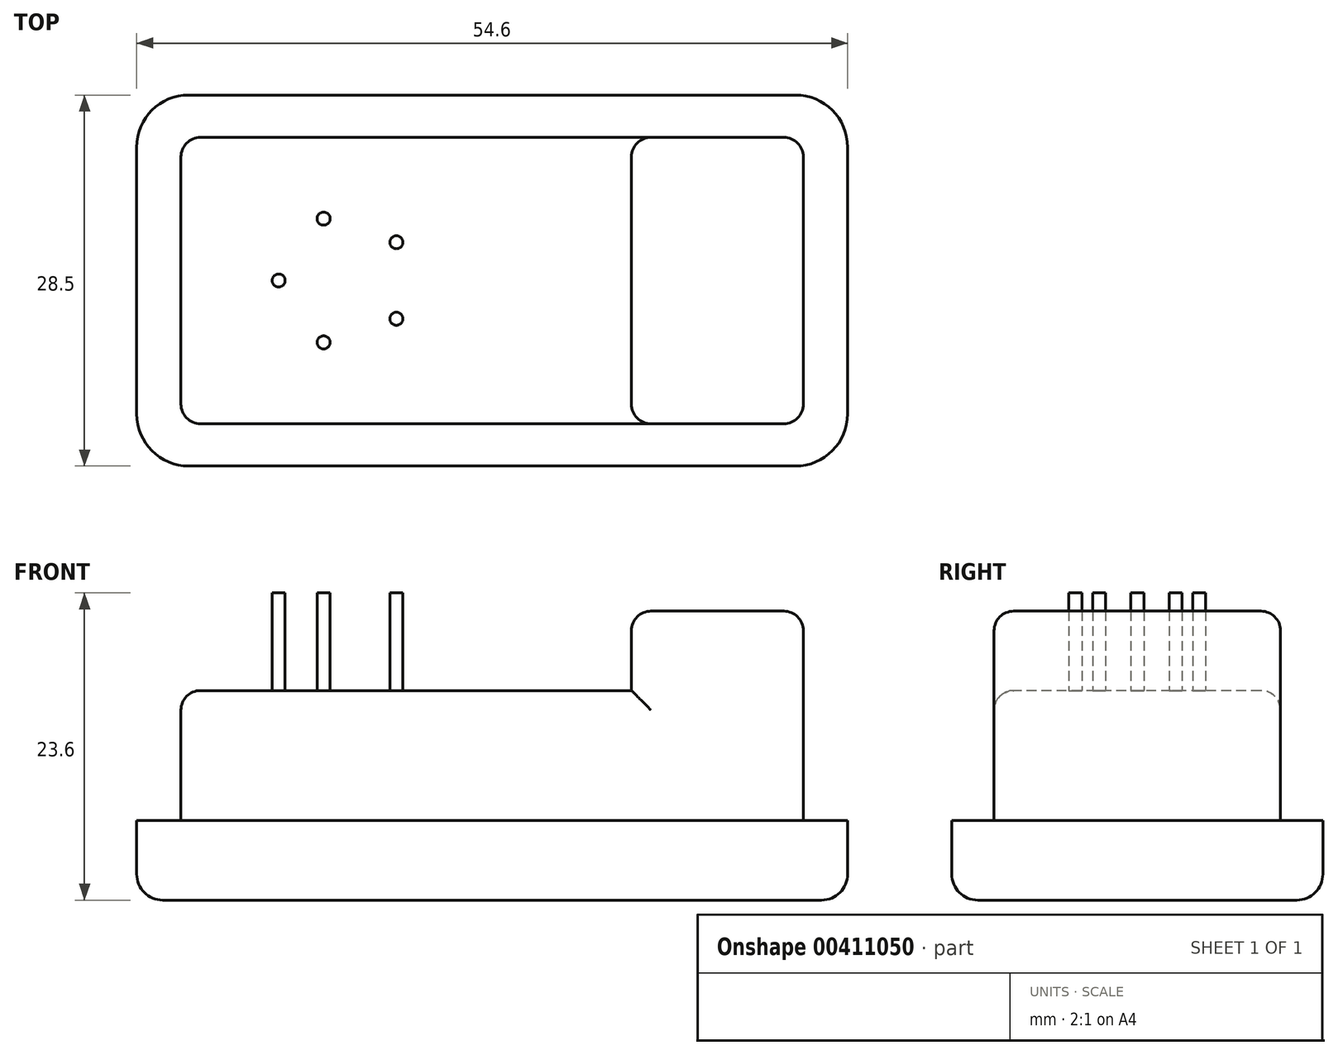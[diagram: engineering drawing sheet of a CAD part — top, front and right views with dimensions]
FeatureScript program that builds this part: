
annotation { "Feature Type Name" : "Feature", "Feature Type Description" : "" }
export const myFeature = defineFeature(function(context is Context, id is Id, definition is map)
    precondition{}
    {
        {
            var Q0;
            Q0=qCreatedBy(makeId("Top.planeOp"),FACE);
            var sketch = newSketch(context, id + "F0", { "sketchPlane" : qUnion([Q0])});
            skLineSegment(sketch, "E0.bottom", {"start": v(0, 28.5) * mm, "end": v(54.6, 28.5) * mm});
            skLineSegment(sketch, "E0.top", {"start": v(0, 0) * mm, "end": v(54.6, 0) * mm});
            skLineSegment(sketch, "E0.left", {"start": v(0, 28.5) * mm, "end": v(0, 0) * mm});
            skLineSegment(sketch, "E0.right", {"start": v(54.6, 28.5) * mm, "end": v(54.6, 0) * mm});
            skSolve(sketch);
        }
        {
            var Q0;
            Q0 = qSketchRegion(id + "F0", true);
            extrude(context, id + "F1", {"entities" : qUnion([Q0]), "depth" : 6.1 * mm});
        }
        {
            var Q0;
            Q0=makeQuery(id+"F1.opExtrude","SWEPT_EDGE",EDGE,{"disambiguationData":[OSD([sQuery(id+"F0.wireOp",EDGE,"E0.top"),sQuery(id+"F0.wireOp",EDGE,"E0.right")])]});
            var Q1;
            Q1=makeQuery(id+"F1.opExtrude","SWEPT_EDGE",EDGE,{"disambiguationData":[OSD([sQuery(id+"F0.wireOp",EDGE,"E0.top"),sQuery(id+"F0.wireOp",EDGE,"E0.left")])]});
            var Q2;
            Q2=makeQuery(id+"F1.opExtrude","SWEPT_EDGE",EDGE,{"disambiguationData":[OSD([sQuery(id+"F0.wireOp",EDGE,"E0.bottom"),sQuery(id+"F0.wireOp",EDGE,"E0.right")])]});
            var Q3;
            Q3=makeQuery(id+"F1.opExtrude","SWEPT_EDGE",EDGE,{"disambiguationData":[OSD([sQuery(id+"F0.wireOp",EDGE,"E0.bottom"),sQuery(id+"F0.wireOp",EDGE,"E0.left")])]});
            fillet(context, id + "F2", {"entities" : qUnion([Q0, Q1, Q2, Q3]), "radius" : 4 * mm, "tangentPropagation" : true, "allowEdgeOverflow" : false});
        }
        {
            var Q0;
            Q0=makeQuery(id+"F1.opExtrude","CAP_EDGE",EDGE,{"disambiguationData":[OSD([sQuery(id+"F0.wireOp",EDGE,"E0.right")])],"isStart":true});
            var Q1;
            {var subQ0=sQuery(id+"F0.wireOp",EDGE,"E0.right");var subQ1=sQuery(id+"F0.wireOp",EDGE,"E0.top");Q1=makeQuery(id+"F2.opFillet","BLEND_EDGE",EDGE,{"blendedFrom":[makeQuery(id+"F1.opExtrude","SWEPT_EDGE",EDGE,{"disambiguationData":[OSD([subQ1,subQ0])]}),makeQuery(id+"F1.opExtrude","CAP_FACE",FACE,{"disambiguationData":[OSD([sQuery(id+"F0.wireOp",EDGE,"E0.bottom"),subQ1,sQuery(id+"F0.wireOp",EDGE,"E0.left"),subQ0])],"isStart":true})],"blendedInto":[makeQuery(id+"F1.opExtrude","CAP_FACE",FACE,{"disambiguationData":[OSD([sQuery(id+"F0.wireOp",EDGE,"E0.bottom"),subQ1,sQuery(id+"F0.wireOp",EDGE,"E0.left"),subQ0])],"isStart":true})]});}
            var Q2;
            Q2=makeQuery(id+"F1.opExtrude","CAP_EDGE",EDGE,{"disambiguationData":[OSD([sQuery(id+"F0.wireOp",EDGE,"E0.top")])],"isStart":true});
            var Q3;
            {var subQ0=sQuery(id+"F0.wireOp",EDGE,"E0.right");var subQ1=sQuery(id+"F0.wireOp",EDGE,"E0.bottom");Q3=makeQuery(id+"F2.opFillet","BLEND_EDGE",EDGE,{"blendedFrom":[makeQuery(id+"F1.opExtrude","SWEPT_EDGE",EDGE,{"disambiguationData":[OSD([subQ1,subQ0])]}),makeQuery(id+"F1.opExtrude","CAP_FACE",FACE,{"disambiguationData":[OSD([subQ1,sQuery(id+"F0.wireOp",EDGE,"E0.top"),sQuery(id+"F0.wireOp",EDGE,"E0.left"),subQ0])],"isStart":true})],"blendedInto":[makeQuery(id+"F1.opExtrude","CAP_FACE",FACE,{"disambiguationData":[OSD([subQ1,sQuery(id+"F0.wireOp",EDGE,"E0.top"),sQuery(id+"F0.wireOp",EDGE,"E0.left"),subQ0])],"isStart":true})]});}
            var Q4;
            {var subQ0=sQuery(id+"F0.wireOp",EDGE,"E0.left");var subQ1=sQuery(id+"F0.wireOp",EDGE,"E0.top");Q4=makeQuery(id+"F2.opFillet","BLEND_EDGE",EDGE,{"blendedFrom":[makeQuery(id+"F1.opExtrude","SWEPT_EDGE",EDGE,{"disambiguationData":[OSD([subQ1,subQ0])]}),makeQuery(id+"F1.opExtrude","CAP_FACE",FACE,{"disambiguationData":[OSD([sQuery(id+"F0.wireOp",EDGE,"E0.bottom"),subQ1,subQ0,sQuery(id+"F0.wireOp",EDGE,"E0.right")])],"isStart":true})],"blendedInto":[makeQuery(id+"F1.opExtrude","CAP_FACE",FACE,{"disambiguationData":[OSD([sQuery(id+"F0.wireOp",EDGE,"E0.bottom"),subQ1,subQ0,sQuery(id+"F0.wireOp",EDGE,"E0.right")])],"isStart":true})]});}
            var Q5;
            Q5=makeQuery(id+"F1.opExtrude","CAP_EDGE",EDGE,{"disambiguationData":[OSD([sQuery(id+"F0.wireOp",EDGE,"E0.left")])],"isStart":true});
            var Q6;
            {var subQ0=sQuery(id+"F0.wireOp",EDGE,"E0.left");var subQ1=sQuery(id+"F0.wireOp",EDGE,"E0.bottom");Q6=makeQuery(id+"F2.opFillet","BLEND_EDGE",EDGE,{"blendedFrom":[makeQuery(id+"F1.opExtrude","SWEPT_EDGE",EDGE,{"disambiguationData":[OSD([subQ1,subQ0])]}),makeQuery(id+"F1.opExtrude","CAP_FACE",FACE,{"disambiguationData":[OSD([subQ1,sQuery(id+"F0.wireOp",EDGE,"E0.top"),subQ0,sQuery(id+"F0.wireOp",EDGE,"E0.right")])],"isStart":true})],"blendedInto":[makeQuery(id+"F1.opExtrude","CAP_FACE",FACE,{"disambiguationData":[OSD([subQ1,sQuery(id+"F0.wireOp",EDGE,"E0.top"),subQ0,sQuery(id+"F0.wireOp",EDGE,"E0.right")])],"isStart":true})]});}
            var Q7;
            Q7=makeQuery(id+"F1.opExtrude","CAP_EDGE",EDGE,{"disambiguationData":[OSD([sQuery(id+"F0.wireOp",EDGE,"E0.bottom")])],"isStart":true});
            fillet(context, id + "F3", {"entities" : qUnion([Q0, Q1, Q2, Q3, Q4, Q5, Q6, Q7]), "radius" : 2 * mm, "tangentPropagation" : true, "allowEdgeOverflow" : false});
        }
        {
            var Q0;
            Q0=makeQuery(id+"F1.opExtrude","CAP_FACE",FACE,{"disambiguationData":[OSD([sQuery(id+"F0.wireOp",EDGE,"E0.bottom"),sQuery(id+"F0.wireOp",EDGE,"E0.top"),sQuery(id+"F0.wireOp",EDGE,"E0.left"),sQuery(id+"F0.wireOp",EDGE,"E0.right")])],"isStart":false});
            var sketch = newSketch(context, id + "F4", { "sketchPlane" : qUnion([Q0])});
            skLineSegment(sketch, "E1.bottom", {"start": v(3.4, 3.25) * mm, "end": v(51.2, 3.25) * mm});
            skLineSegment(sketch, "E1.top", {"start": v(3.4, 25.25) * mm, "end": v(51.2, 25.25) * mm});
            skLineSegment(sketch, "E1.left", {"start": v(3.4, 3.25) * mm, "end": v(3.4, 25.25) * mm});
            skLineSegment(sketch, "E1.right", {"start": v(51.2, 3.25) * mm, "end": v(51.2, 25.25) * mm});
            skPoint(sketch, "E2", {"position": v(27.3, 25.25) * mm});
            skPoint(sketch, "E3", {"position": v(3.4, 14.25) * mm});
            skSolve(sketch);
        }
        {
            var Q0;
            Q0 = qSketchRegion(id + "F4", true);
            extrude(context, id + "F5", {"entities" : qUnion([Q0]), "operationType" : NewBodyOperationType.ADD, "depth" : 10 * mm});
        }
        {
            var Q0;
            Q0=makeQuery(id+"F5.opExtrude","CAP_FACE",FACE,{"disambiguationData":[OSD([sQuery(id+"F4.wireOp",EDGE,"E1.bottom"),sQuery(id+"F4.wireOp",EDGE,"E1.top"),sQuery(id+"F4.wireOp",EDGE,"E1.left"),sQuery(id+"F4.wireOp",EDGE,"E1.right")])],"isStart":false});
            var sketch = newSketch(context, id + "F6", { "sketchPlane" : qUnion([Q0])});
            skLineSegment(sketch, "E4.bottom", {"start": v(51.2, 25.25) * mm, "end": v(38, 25.25) * mm});
            skLineSegment(sketch, "E4.top", {"start": v(51.2, 3.25) * mm, "end": v(38, 3.25) * mm});
            skLineSegment(sketch, "E4.left", {"start": v(51.2, 25.25) * mm, "end": v(51.2, 3.25) * mm});
            skLineSegment(sketch, "E4.right", {"start": v(38, 25.25) * mm, "end": v(38, 3.25) * mm});
            skSolve(sketch);
        }
        {
            var Q0;
            Q0=makeQuery(id+"F6.imprint","IMPRINT",FACE,{"disambiguationData":[TD([[makeQuery(id+"F6.imprint","IMPRINT",EDGE,{"derivedFrom":sQuery(id+"F6.wireOp",EDGE,"E4.bottom")}),-1.0]])]});
            extrude(context, id + "F7", {"entities" : qUnion([Q0]), "operationType" : NewBodyOperationType.ADD, "depth" : 6.1 * mm});
        }
        {
            var Q0;
            Q0=makeQuery(id+"F5.opExtrude","SWEPT_EDGE",EDGE,{"disambiguationData":[OSD([sQuery(id+"F4.wireOp",EDGE,"E1.bottom"),sQuery(id+"F4.wireOp",EDGE,"E1.left")])]});
            var Q1;
            Q1=makeQuery(id+"F5.opExtrude","CAP_EDGE",EDGE,{"disambiguationData":[OSD([sQuery(id+"F4.wireOp",EDGE,"E1.bottom")])],"isStart":false});
            var Q2;
            Q2=makeQuery(id+"F7.opExtrude","SWEPT_EDGE",EDGE,{"disambiguationData":[OSD([sQuery(id+"F4.wireOp",EDGE,"E1.bottom"),sQuery(id+"F6.wireOp",EDGE,"E4.top"),sQuery(id+"F6.wireOp",EDGE,"E4.right")])]});
            var Q3;
            Q3=makeQuery(id+"F7.opExtrude","CAP_EDGE",EDGE,{"disambiguationData":[OSD([sQuery(id+"F6.wireOp",EDGE,"E4.top")])],"isStart":false});
            var Q4;
            Q4=makeQuery(id+"F7.boolean.opBoolean","MERGE",EDGE,{"derivedFrom":[makeQuery(id+"F5.opExtrude","SWEPT_EDGE",EDGE,{"disambiguationData":[OSD([sQuery(id+"F4.wireOp",EDGE,"E1.bottom"),sQuery(id+"F4.wireOp",EDGE,"E1.right")])]}),makeQuery(id+"F7.opExtrude","SWEPT_EDGE",EDGE,{"disambiguationData":[OSD([sQuery(id+"F6.wireOp",EDGE,"E4.top"),sQuery(id+"F6.wireOp",EDGE,"E4.left")])]})]});
            var Q5;
            Q5=makeQuery(id+"F7.opExtrude","CAP_EDGE",EDGE,{"disambiguationData":[OSD([sQuery(id+"F6.wireOp",EDGE,"E4.left")])],"isStart":false});
            var Q6;
            Q6=makeQuery(id+"F7.opExtrude","CAP_EDGE",EDGE,{"disambiguationData":[OSD([sQuery(id+"F6.wireOp",EDGE,"E4.right")])],"isStart":false});
            var Q7;
            Q7=makeQuery(id+"F7.opExtrude","CAP_EDGE",EDGE,{"disambiguationData":[OSD([sQuery(id+"F6.wireOp",EDGE,"E4.bottom")])],"isStart":false});
            var Q8;
            Q8=makeQuery(id+"F7.boolean.opBoolean","MERGE",EDGE,{"derivedFrom":[makeQuery(id+"F5.opExtrude","SWEPT_EDGE",EDGE,{"disambiguationData":[OSD([sQuery(id+"F4.wireOp",EDGE,"E1.top"),sQuery(id+"F4.wireOp",EDGE,"E1.right")])]}),makeQuery(id+"F7.opExtrude","SWEPT_EDGE",EDGE,{"disambiguationData":[OSD([sQuery(id+"F6.wireOp",EDGE,"E4.bottom"),sQuery(id+"F6.wireOp",EDGE,"E4.left")])]})]});
            var Q9;
            Q9=makeQuery(id+"F5.opExtrude","CAP_EDGE",EDGE,{"disambiguationData":[OSD([sQuery(id+"F4.wireOp",EDGE,"E1.top")])],"isStart":false});
            var Q10;
            Q10=makeQuery(id+"F5.opExtrude","CAP_EDGE",EDGE,{"disambiguationData":[OSD([sQuery(id+"F4.wireOp",EDGE,"E1.left")])],"isStart":false});
            var Q11;
            Q11=makeQuery(id+"F7.opExtrude","SWEPT_EDGE",EDGE,{"disambiguationData":[OSD([sQuery(id+"F4.wireOp",EDGE,"E1.top"),sQuery(id+"F6.wireOp",EDGE,"E4.bottom"),sQuery(id+"F6.wireOp",EDGE,"E4.right")])]});
            var Q12;
            Q12=makeQuery(id+"F5.opExtrude","SWEPT_EDGE",EDGE,{"disambiguationData":[OSD([sQuery(id+"F4.wireOp",EDGE,"E1.top"),sQuery(id+"F4.wireOp",EDGE,"E1.left")])]});
            fillet(context, id + "F8", {"entities" : qUnion([Q0, Q1, Q2, Q3, Q4, Q5, Q6, Q7, Q8, Q9, Q10, Q11, Q12]), "radius" : 1.5 * mm, "tangentPropagation" : true, "allowEdgeOverflow" : false});
        }
        {
            var Q0;
            Q0=makeQuery(id+"F5.opExtrude","CAP_FACE",FACE,{"disambiguationData":[OSD([sQuery(id+"F4.wireOp",EDGE,"E1.bottom"),sQuery(id+"F4.wireOp",EDGE,"E1.top"),sQuery(id+"F4.wireOp",EDGE,"E1.left"),sQuery(id+"F4.wireOp",EDGE,"E1.right")])],"isStart":false});
            var sketch = newSketch(context, id + "F9", { "sketchPlane" : qUnion([Q0])});
            skCircle(sketch, "E5", {"center": v(15.9, 14.25) * mm, "radius": 5 * mm, "construction": true});
            skCircle(sketch, "E6", {"center": v(10.9, 14.25) * mm, "radius": 0.5 * mm});
            skCircle(sketch, "E7.1.0", {"center": v(14.35, 9.5) * mm, "radius": 0.5 * mm});
            skCircle(sketch, "E7.2.0", {"center": v(19.95, 11.31) * mm, "radius": 0.5 * mm});
            skCircle(sketch, "E8.1.3.0", {"center": v(19.95, 17.19) * mm, "radius": 0.5 * mm});
            skCircle(sketch, "E8.1.4.0", {"center": v(14.35, 19) * mm, "radius": 0.5 * mm});
            skSolve(sketch);
        }
        {
            var Q0;
            Q0 = qSketchRegion(id + "F9", true);
            extrude(context, id + "F10", {"entities" : qUnion([Q0]), "operationType" : NewBodyOperationType.ADD, "depth" : 7.5 * mm});
        }
    });
